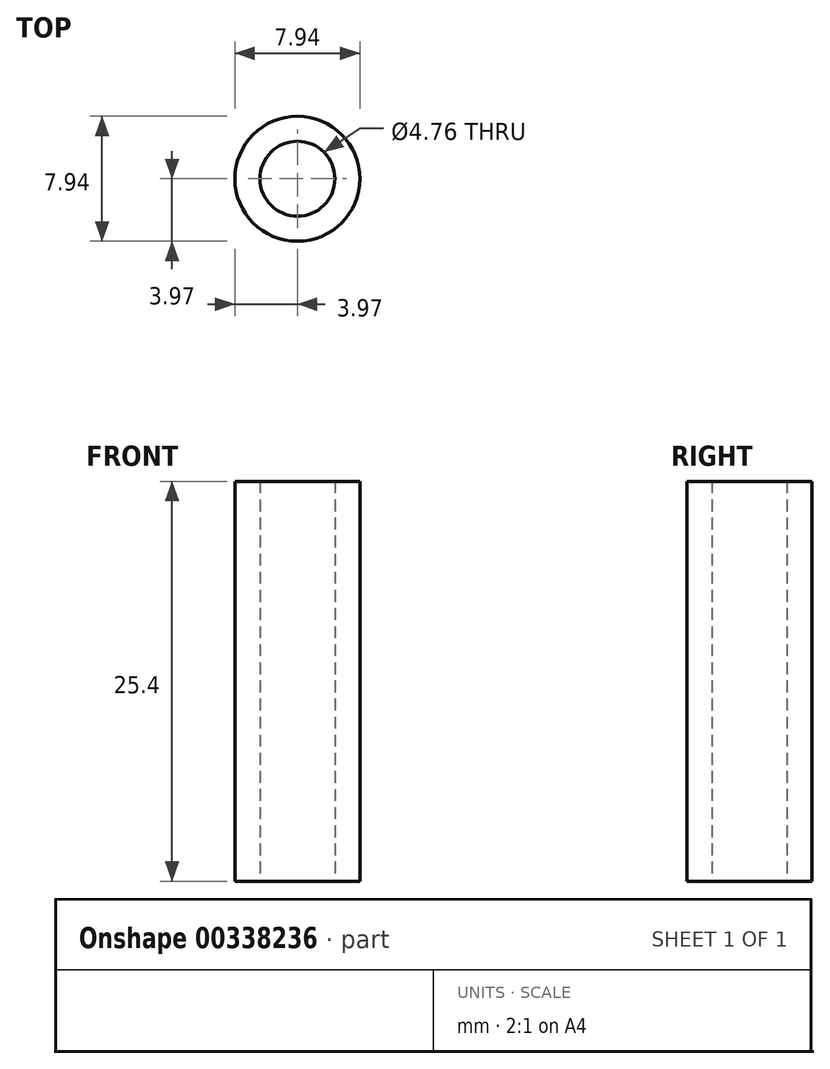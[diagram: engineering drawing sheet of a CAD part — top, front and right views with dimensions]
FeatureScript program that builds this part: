
annotation { "Feature Type Name" : "Feature", "Feature Type Description" : "" }
export const myFeature = defineFeature(function(context is Context, id is Id, definition is map)
    precondition{}
    {
        {
            var Q0;
            Q0=qCreatedBy(makeId("Top.planeOp"),FACE);
            var sketch = newSketch(context, id + "F0", { "sketchPlane" : qUnion([Q0])});
            skCircle(sketch, "E0", {"center": v(0, 0) * mm, "radius": 2.38 * mm});
            skCircle(sketch, "E1", {"center": v(0, 0) * mm, "radius": 3.97 * mm});
            skSolve(sketch);
        }
        {
            var Q0;
            Q0=qSketchRegion(id+"F0",true);
            extrude(context, id + "F1", {"entities" : qUnion([Q0]), "depth" : 25.4 * mm});
        }
    });
